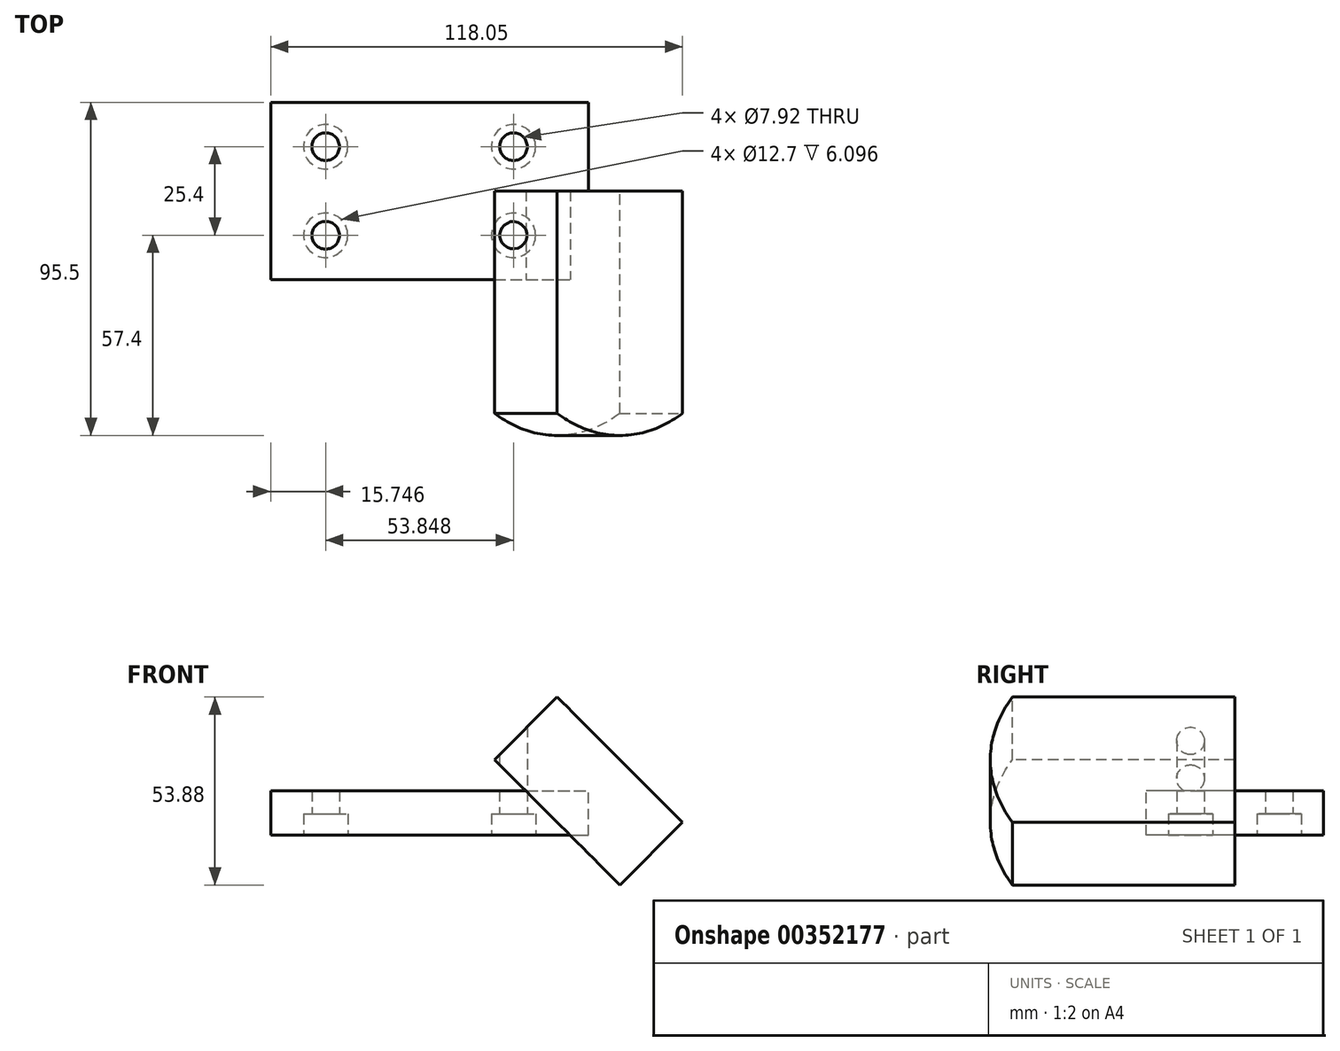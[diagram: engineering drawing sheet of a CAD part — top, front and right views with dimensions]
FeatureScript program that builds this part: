
annotation { "Feature Type Name" : "Feature", "Feature Type Description" : "" }
export const myFeature = defineFeature(function(context is Context, id is Id, definition is map)
    precondition{}
    {
        {
            var Q0;
            Q0=qCreatedBy(makeId("Top.planeOp"),FACE);
            var sketch = newSketch(context, id + "F0", { "sketchPlane" : qUnion([Q0])});
            skLineSegment(sketch, "E0.bottom", {"start": v(-91.11, 25.4) * mm, "end": v(0, 25.4) * mm});
            skLineSegment(sketch, "E0.top", {"start": v(-91.11, -25.4) * mm, "end": v(0, -25.4) * mm});
            skLineSegment(sketch, "E0.left", {"start": v(-91.11, 25.4) * mm, "end": v(-91.11, -25.4) * mm});
            skLineSegment(sketch, "E0.right", {"start": v(0, 25.4) * mm, "end": v(0, -25.4) * mm});
            skSolve(sketch);
        }
        {
            var Q0;
            Q0=sQuery(id+"F0.wireOp",EDGE,"E0.right");
            cPlane(context, id + "F1", {"entities" : qUnion([Q0]), "cplaneType" : CPlaneType.LINE_ANGLE, "offset" : 25.4 * mm, "angle" : 45 * degree, "oppositeDirection" : true, "width" : 152.4 * mm, "height" : 152.4 * mm});
        }
        {
            var Q0;
            Q0=qCreatedBy(id+"F1.planeOp",FACE);
            var sketch = newSketch(context, id + "F2", { "sketchPlane" : qUnion([Q0])});
            skLineSegment(sketch, "E1", {"start": v(0, 25.4) * mm, "end": v(0, -25.4) * mm});
            skLineSegment(sketch, "E2", {"start": v(0, 25.4) * mm, "end": v(63.74, 25.4) * mm});
            skLineSegment(sketch, "E3", {"start": v(63.74, -25.4) * mm, "end": v(0, -25.4) * mm});
            skArc(sketch, "E4", {"start": v(63.74, -25.4) * mm, "mid": v(70.1, 0) * mm, "end": v(63.74, 25.4) * mm});
            skPoint(sketch, "E5", {"position": v(70.1, 0) * mm});
            skSolve(sketch);
        }
        {
            var Q0;
            Q0=makeQuery(id+"F0.imprint","IMPRINT",FACE,{"disambiguationData":[TD([[makeQuery(id+"F0.imprint","IMPRINT",EDGE,{"derivedFrom":sQuery(id+"F0.wireOp",EDGE,"E0.bottom")}),-1.0]])]});
            extrude(context, id + "F3", {"entities" : qUnion([Q0]), "oppositeDirection" : true, "depth" : 12.7 * mm});
        }
        {
            var Q0;
            Q0=makeQuery(id+"F2.imprint","IMPRINT",FACE,{"disambiguationData":[TD([[makeQuery(id+"F2.imprint","IMPRINT",EDGE,{"derivedFrom":sQuery(id+"F2.wireOp",EDGE,"E1")}),1.0]])]});
            var Q1;
            Q1=makeQuery(id+"F3.opExtrude","CAP_VERTEX",VERTEX,{"disambiguationData":[OSD([sQuery(id+"F0.wireOp",EDGE,"E0.top"),sQuery(id+"F0.wireOp",EDGE,"E0.right")])],"isStart":false});
            extrude(context, id + "F4", {"entities" : qUnion([Q0]), "operationType" : NewBodyOperationType.ADD, "endBoundEntityVertex" : qUnion([Q1]), "depth" : 25.4 * mm, "hasSecondDirection" : true, "secondDirectionOppositeDirection" : true, "secondDirectionDepth" : 12.7 * mm, "symmetric" : true});
        }
        {
            var Q0;
            Q0=makeQuery(id+"F4.opExtrude","SWEPT_FACE",FACE,{"disambiguationData":[OSD([sQuery(id+"F2.wireOp",EDGE,"E1")])]});
            var sketch = newSketch(context, id + "F5", { "sketchPlane" : qUnion([Q0])});
            skLineSegment(sketch, "E6", {"start": v(-25.4, 0) * mm, "end": v(25.4, 0) * mm});
            skLineSegment(sketch, "E7", {"start": v(25.4, 0) * mm, "end": v(25.4, 12.7) * mm});
            skLineSegment(sketch, "E8", {"start": v(25.4, 12.7) * mm, "end": v(-25.4, 12.7) * mm});
            skLineSegment(sketch, "E9", {"start": v(-25.4, 12.7) * mm, "end": v(-25.4, 0) * mm});
            skLineSegment(sketch, "E10", {"start": v(-9.65, 12.79) * mm, "end": v(-9.65, 6.69) * mm});
            skLineSegment(sketch, "E11", {"start": v(-9.65, 6.69) * mm, "end": v(-15.75, 6.69) * mm});
            skLineSegment(sketch, "E12", {"start": v(-15.75, 6.69) * mm, "end": v(-15.75, 0) * mm});
            skLineSegment(sketch, "E13", {"start": v(-15.75, 0) * mm, "end": v(15.75, 0) * mm});
            skLineSegment(sketch, "E14", {"start": v(15.75, 0) * mm, "end": v(15.75, 6.69) * mm});
            skLineSegment(sketch, "E15", {"start": v(15.75, 6.69) * mm, "end": v(9.65, 6.69) * mm});
            skLineSegment(sketch, "E16", {"start": v(9.65, 6.69) * mm, "end": v(9.65, 12.7) * mm});
            skLineSegment(sketch, "E17", {"start": v(-9.65, 12.79) * mm, "end": v(9.65, 12.7) * mm});
            skPoint(sketch, "E18", {"position": v(0, 0) * mm});
            skPoint(sketch, "E19", {"position": v(0, 12.74) * mm});
            skSolve(sketch);
        }
        {
            var Q0;
            {var subQ0=sQuery(id+"F5.wireOp",EDGE,"E11");Q0=makeQuery(id+"F5.imprint","IMPRINT",FACE,{"disambiguationData":[TD([[makeQuery(id+"F5.imprint","IMPRINT",EDGE,{"derivedFrom":subQ0}),1.0]])]});}
            extrude(context, id + "F6", {"entities" : qUnion([Q0]), "operationType" : NewBodyOperationType.REMOVE, "endBound" : BoundingType.THROUGH_ALL, "oppositeDirection" : true, "depth" : 25.4 * mm});
        }
        {
            var Q0;
            {var subQ4=sQuery(id+"F5.wireOp",EDGE,"E9");Q0=makeQuery(id+"F5.imprint","IMPRINT",FACE,{"disambiguationData":[TD([[makeQuery(id+"F5.imprint","IMPRINT",EDGE,{"derivedFrom":subQ4}),-1.0]])]});}
            var Q1;
            {var subQ1=sQuery(id+"F5.wireOp",EDGE,"E7");Q1=makeQuery(id+"F5.imprint","IMPRINT",FACE,{"disambiguationData":[TD([[makeQuery(id+"F5.imprint","IMPRINT",EDGE,{"derivedFrom":subQ1}),1.0]])]});}
            extrude(context, id + "F7", {"entities" : qUnion([Q0, Q1]), "operationType" : NewBodyOperationType.REMOVE, "oppositeDirection" : true, "depth" : 12.7 * mm});
        }
        {
            var Q0;
            Q0=makeQuery(id+"F3.opExtrude","CAP_FACE",FACE,{"disambiguationData":[OSD([sQuery(id+"F0.wireOp",EDGE,"E0.bottom"),sQuery(id+"F0.wireOp",EDGE,"E0.top"),sQuery(id+"F0.wireOp",EDGE,"E0.left"),sQuery(id+"F0.wireOp",EDGE,"E0.right")])],"isStart":false});
            var sketch = newSketch(context, id + "F8", { "sketchPlane" : qUnion([Q0])});
            skLineSegment(sketch, "E20.bottom", {"start": v(-91.11, 25.4) * mm, "end": v(-5.26, 25.4) * mm});
            skLineSegment(sketch, "E20.top", {"start": v(-91.11, -25.4) * mm, "end": v(-5.26, -25.4) * mm});
            skLineSegment(sketch, "E20.left", {"start": v(-91.11, 25.4) * mm, "end": v(-91.11, -25.4) * mm});
            skLineSegment(sketch, "E20.right", {"start": v(-5.26, 25.4) * mm, "end": v(-5.26, -25.4) * mm});
            skPoint(sketch, "E21", {"position": v(-75.36, 12.7) * mm});
            skPoint(sketch, "E22", {"position": v(-21.52, 12.7) * mm});
            skPoint(sketch, "E23", {"position": v(-75.36, -12.7) * mm});
            skPoint(sketch, "E24", {"position": v(-21.52, -12.7) * mm});
            skSolve(sketch);
        }
        {
            var Q0;
            Q0=sQuery(id+"F8.wireOp",VERTEX,"E21");
            var Q1;
            Q1=sQuery(id+"F8.wireOp",VERTEX,"E23");
            var Q2;
            Q2=sQuery(id+"F8.wireOp",VERTEX,"E22");
            var Q3;
            Q3=sQuery(id+"F8.wireOp",VERTEX,"E24");
            var Q4;
            Q4=makeQuery(id+"F3.opExtrude","SWEPT_BODY",BODY,{"disambiguationData":[OSD([sQuery(id+"F0.wireOp",EDGE,"E0.bottom"),sQuery(id+"F0.wireOp",EDGE,"E0.top"),sQuery(id+"F0.wireOp",EDGE,"E0.left"),sQuery(id+"F0.wireOp",EDGE,"E0.right")])]});
            hole(context, id + "F9", {"style" : HoleStyle.C_BORE, "endStyle" : HoleEndStyle.THROUGH, "holeDiameter" : 7.92 * mm, "cBoreDiameter" : 12.7 * mm, "cBoreDepth" : 6.1 * mm, "isTappedThrough" : true, "tappedDepth" : 12.7 * mm, "tapClearance" : 3, "locations" : qUnion([Q0, Q1, Q2, Q3]), "scope" : qUnion([Q4])});
        }
    });
